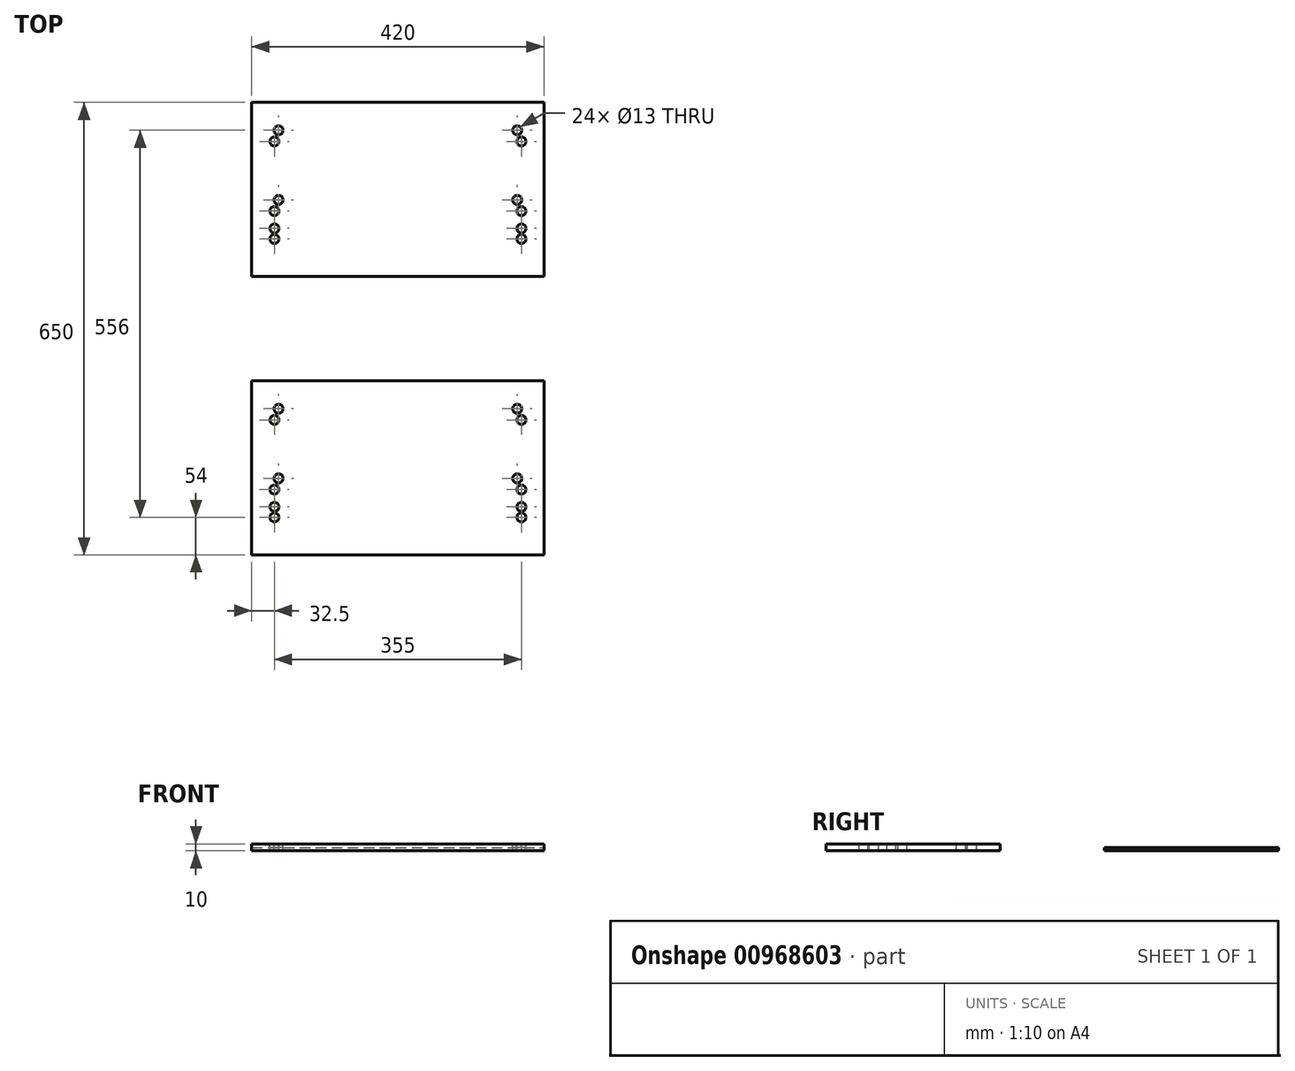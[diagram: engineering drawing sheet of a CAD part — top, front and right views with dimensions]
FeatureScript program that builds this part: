
annotation { "Feature Type Name" : "Feature", "Feature Type Description" : "" }
export const myFeature = defineFeature(function(context is Context, id is Id, definition is map)
    precondition{}
    {
        {
            var Q0;
            Q0=qCreatedBy(makeId("Top.planeOp"),FACE);
            var sketch = newSketch(context, id + "F0", { "sketchPlane" : qUnion([Q0])});
            skLineSegment(sketch, "E0.bottom", {"start": v(0, 0) * mm, "end": v(420, 0) * mm});
            skLineSegment(sketch, "E0.top", {"start": v(0, 250) * mm, "end": v(420, 250) * mm});
            skLineSegment(sketch, "E0.left", {"start": v(0, 0) * mm, "end": v(0, 250) * mm});
            skLineSegment(sketch, "E0.right", {"start": v(420, 0) * mm, "end": v(420, 250) * mm});
            skSolve(sketch);
        }
        {
            var Q0;
            Q0=makeQuery(id+"F0.imprint","IMPRINT",FACE,{"disambiguationData":[TD([[makeQuery(id+"F0.imprint","IMPRINT",EDGE,{"derivedFrom":sQuery(id+"F0.wireOp",EDGE,"E0.bottom")}),1.0]])]});
            extrude(context, id + "F1", {"entities" : qUnion([Q0]), "depth" : 10 * mm, "offsetDistance" : 25 * mm});
        }
        {
            var Q0;
            Q0=makeQuery(id+"F1.opExtrude","CAP_FACE",FACE,{"disambiguationData":[OSD([sQuery(id+"F0.wireOp",EDGE,"E0.bottom"),sQuery(id+"F0.wireOp",EDGE,"E0.top"),sQuery(id+"F0.wireOp",EDGE,"E0.left"),sQuery(id+"F0.wireOp",EDGE,"E0.right")])],"isStart":false});
            var sketch = newSketch(context, id + "F2", { "sketchPlane" : qUnion([Q0])});
            skLineSegment(sketch, "E1", {"start": v(210, 250) * mm, "end": v(210, 0) * mm, "construction": true});
            skLineSegment(sketch, "E2.bottom", {"start": v(38.5, 210) * mm, "end": v(381.5, 210) * mm, "construction": true});
            skLineSegment(sketch, "E2.top", {"start": v(38.5, 110) * mm, "end": v(381.5, 110) * mm, "construction": true});
            skLineSegment(sketch, "E2.left", {"start": v(38.5, 210) * mm, "end": v(38.5, 110) * mm, "construction": true});
            skLineSegment(sketch, "E2.right", {"start": v(381.5, 210) * mm, "end": v(381.5, 110) * mm, "construction": true});
            skSolve(sketch);
        }
        {
            var Q0;
            Q0=sQuery(id+"F2.wireOp",VERTEX,"E2.bottom.start");
            var Q1;
            Q1=sQuery(id+"F2.wireOp",VERTEX,"E2.bottom.end");
            var Q2;
            Q2=sQuery(id+"F2.wireOp",VERTEX,"E2.top.end");
            var Q3;
            Q3=sQuery(id+"F2.wireOp",VERTEX,"E2.top.start");
            var Q4;
            Q4=makeQuery(id+"F1.opExtrude","SWEPT_BODY",BODY,{"disambiguationData":[OSD([sQuery(id+"F0.wireOp",EDGE,"E0.bottom"),sQuery(id+"F0.wireOp",EDGE,"E0.top"),sQuery(id+"F0.wireOp",EDGE,"E0.left"),sQuery(id+"F0.wireOp",EDGE,"E0.right")])]});
            hole(context, id + "F3", {"style" : HoleStyle.SIMPLE, "endStyle" : HoleEndStyle.THROUGH, "holeDiameter" : 13 * mm, "majorDiameter" : 5 * mm, "isTappedThrough" : true, "tappedDepth" : 12 * mm, "tapClearance" : 3, "locations" : qUnion([Q0, Q1, Q2, Q3]), "scope" : qUnion([Q4])});
        }
        {
            var Q0;
            Q0=makeQuery(id+"F1.opExtrude","CAP_FACE",FACE,{"disambiguationData":[OSD([sQuery(id+"F0.wireOp",EDGE,"E0.bottom"),sQuery(id+"F0.wireOp",EDGE,"E0.top"),sQuery(id+"F0.wireOp",EDGE,"E0.left"),sQuery(id+"F0.wireOp",EDGE,"E0.right")])],"isStart":false});
            var sketch = newSketch(context, id + "F4", { "sketchPlane" : qUnion([Q0])});
            skLineSegment(sketch, "E3", {"start": v(210, 250) * mm, "end": v(210, 0) * mm, "construction": true});
            skLineSegment(sketch, "E4.bottom", {"start": v(32.5, 194) * mm, "end": v(387.5, 194) * mm, "construction": true});
            skLineSegment(sketch, "E4.top", {"start": v(32.5, 94) * mm, "end": v(387.5, 94) * mm, "construction": true});
            skLineSegment(sketch, "E4.left", {"start": v(32.5, 194) * mm, "end": v(32.5, 94) * mm, "construction": true});
            skLineSegment(sketch, "E4.right", {"start": v(387.5, 194) * mm, "end": v(387.5, 94) * mm, "construction": true});
            skLineSegment(sketch, "E5", {"start": v(32.5, 69) * mm, "end": v(387.5, 69) * mm, "construction": true});
            skSolve(sketch);
        }
        {
            var Q0;
            Q0=sQuery(id+"F4.wireOp",VERTEX,"E4.bottom.start");
            var Q1;
            Q1=sQuery(id+"F4.wireOp",VERTEX,"E4.bottom.end");
            var Q2;
            Q2=sQuery(id+"F4.wireOp",VERTEX,"E4.top.end");
            var Q3;
            Q3=sQuery(id+"F4.wireOp",VERTEX,"E5.end");
            var Q4;
            Q4=sQuery(id+"F4.wireOp",VERTEX,"E5.start");
            var Q5;
            Q5=sQuery(id+"F4.wireOp",VERTEX,"E4.top.start");
            var Q6;
            Q6=makeQuery(id+"F1.opExtrude","SWEPT_BODY",BODY,{"disambiguationData":[OSD([sQuery(id+"F0.wireOp",EDGE,"E0.bottom"),sQuery(id+"F0.wireOp",EDGE,"E0.top"),sQuery(id+"F0.wireOp",EDGE,"E0.left"),sQuery(id+"F0.wireOp",EDGE,"E0.right")])]});
            hole(context, id + "F5", {"style" : HoleStyle.SIMPLE, "endStyle" : HoleEndStyle.THROUGH, "holeDiameter" : 13 * mm, "majorDiameter" : 5 * mm, "isTappedThrough" : true, "tappedDepth" : 12 * mm, "tapClearance" : 3, "locations" : qUnion([Q0, Q1, Q2, Q3, Q4, Q5]), "scope" : qUnion([Q6])});
        }
        {
            var Q0;
            Q0=makeQuery(id+"F1.opExtrude","CAP_FACE",FACE,{"disambiguationData":[OSD([sQuery(id+"F0.wireOp",EDGE,"E0.bottom"),sQuery(id+"F0.wireOp",EDGE,"E0.top"),sQuery(id+"F0.wireOp",EDGE,"E0.left"),sQuery(id+"F0.wireOp",EDGE,"E0.right")])],"isStart":false});
            var sketch = newSketch(context, id + "F6", { "sketchPlane" : qUnion([Q0])});
            skLineSegment(sketch, "E6", {"start": v(210, 250) * mm, "end": v(210, 0) * mm, "construction": true});
            skLineSegment(sketch, "E7.bottom", {"start": v(32.5, 194) * mm, "end": v(387.5, 194) * mm, "construction": true});
            skLineSegment(sketch, "E7.top", {"start": v(32.5, 54) * mm, "end": v(387.5, 54) * mm, "construction": true});
            skLineSegment(sketch, "E7.left", {"start": v(32.5, 194) * mm, "end": v(32.5, 54) * mm, "construction": true});
            skLineSegment(sketch, "E7.right", {"start": v(387.5, 194) * mm, "end": v(387.5, 54) * mm, "construction": true});
            skSolve(sketch);
        }
        {
            var Q0;
            Q0=sQuery(id+"F6.wireOp",VERTEX,"E7.bottom.start");
            var Q1;
            Q1=sQuery(id+"F6.wireOp",VERTEX,"E7.bottom.end");
            var Q2;
            Q2=sQuery(id+"F6.wireOp",VERTEX,"E7.top.end");
            var Q3;
            Q3=sQuery(id+"F6.wireOp",VERTEX,"E7.top.start");
            var Q4;
            Q4=makeQuery(id+"F1.opExtrude","SWEPT_BODY",BODY,{"disambiguationData":[OSD([sQuery(id+"F0.wireOp",EDGE,"E0.bottom"),sQuery(id+"F0.wireOp",EDGE,"E0.top"),sQuery(id+"F0.wireOp",EDGE,"E0.left"),sQuery(id+"F0.wireOp",EDGE,"E0.right")])]});
            hole(context, id + "F7", {"style" : HoleStyle.SIMPLE, "endStyle" : HoleEndStyle.THROUGH, "holeDiameter" : 13 * mm, "majorDiameter" : 5 * mm, "isTappedThrough" : true, "tappedDepth" : 12 * mm, "tapClearance" : 3, "locations" : qUnion([Q0, Q1, Q2, Q3]), "scope" : qUnion([Q4])});
        }
        {
            var Q0;
            Q0=makeQuery(id+"F1.opExtrude","SWEPT_BODY",BODY,{"disambiguationData":[OSD([sQuery(id+"F0.wireOp",EDGE,"E0.bottom"),sQuery(id+"F0.wireOp",EDGE,"E0.top"),sQuery(id+"F0.wireOp",EDGE,"E0.left"),sQuery(id+"F0.wireOp",EDGE,"E0.right")])]});
            transform(context, id + "F8", {"entities" : qUnion([Q0]), "transformType" : TransformType.TRANSLATION_3D, "dx" : 0 * mm, "dy" : 400 * mm, "dz" : 0 * mm, "makeCopy" : true});
        }
        {
            var Q0;
            Q0=makeQuery(id+"F8.opPattern","COPY",FACE,{"derivedFrom":makeQuery(id+"F1.opExtrude","CAP_FACE",FACE,{"disambiguationData":[OSD([sQuery(id+"F0.wireOp",EDGE,"E0.bottom"),sQuery(id+"F0.wireOp",EDGE,"E0.top"),sQuery(id+"F0.wireOp",EDGE,"E0.left"),sQuery(id+"F0.wireOp",EDGE,"E0.right")])],"isStart":false}),"instanceName":"1"});
            var sketch = newSketch(context, id + "F9", { "sketchPlane" : qUnion([Q0])});
            skLineSegment(sketch, "E8.0.0", {"start": v(420, 650) * mm, "end": v(0, 650) * mm});
            skLineSegment(sketch, "E8.0.1", {"start": v(0, 650) * mm, "end": v(0, 400) * mm});
            skLineSegment(sketch, "E8.0.2", {"start": v(0, 400) * mm, "end": v(420, 400) * mm});
            skLineSegment(sketch, "E8.0.3", {"start": v(420, 400) * mm, "end": v(420, 650) * mm});
            skSolve(sketch);
        }
        {
            var Q0;
            Q0=makeQuery(id+"F9.imprint","IMPRINT",FACE,{"disambiguationData":[TD([[makeQuery(id+"F9.imprint","IMPRINT",EDGE,{"derivedFrom":sQuery(id+"F9.wireOp",EDGE,"E8.0.0")}),-1.0]])]});
            extrude(context, id + "F10", {"entities" : qUnion([Q0]), "operationType" : NewBodyOperationType.REMOVE, "oppositeDirection" : true, "depth" : 5.2 * mm, "offsetDistance" : 25 * mm});
        }
    });
